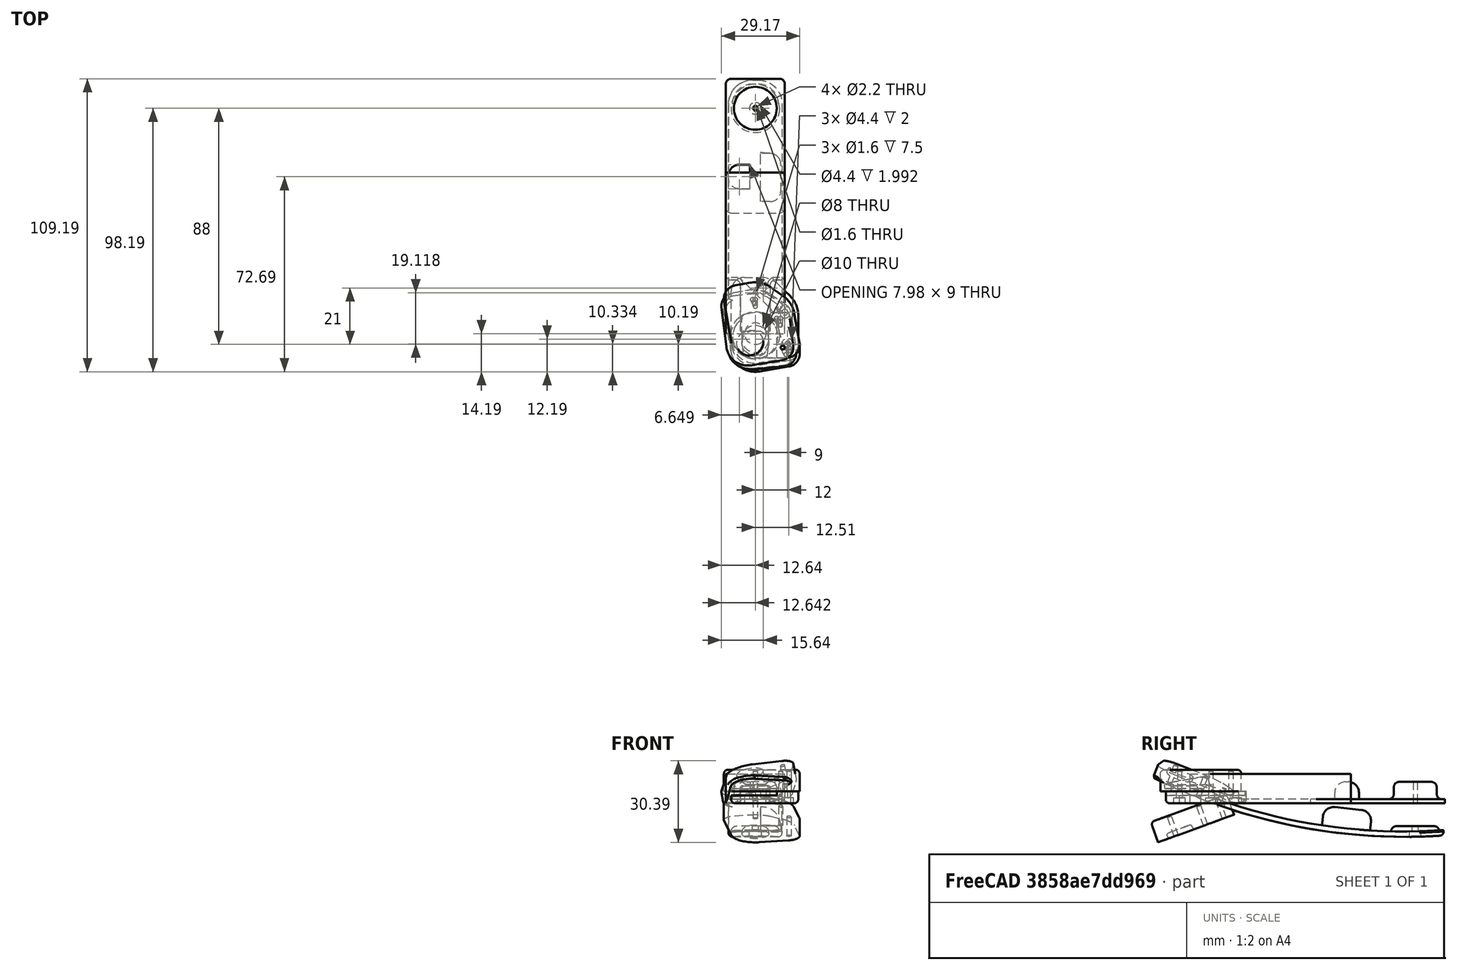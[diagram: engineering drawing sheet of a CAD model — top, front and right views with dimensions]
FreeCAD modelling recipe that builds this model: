
FCSTD DOCUMENT  (FreeCAD 1.0R38641 +678 (Git))
Label: HelmetVisir
License: All rights reserved
LicenseURL: https://en.wikipedia.org/wiki/All_rights_reserved
objects: Part::Fillet×37, Part::Cylinder×19, Part::Box×13, Part::MultiFuse×10, Part::Cut×10, Part::Chamfer×6, Part::Feature×4, Part::MultiCommon×1, Part::Mirroring×1
note: 101 computed .brp shape members not serialized (recipe doc carries the construction recipe); baked Part::Feature solids carry a one-line shape summary decoded from their .brp

FEATURE [Part::Cylinder] Cylinder012  label="Magnet001"
  Angle = 360
  AttacherType = Attacher::AttachEngine3D
  FirstAngle = 0
  Height = 6.5
  Radius = 5
  SecondAngle = 0
FEATURE [Part::Cylinder] Cylinder014  label="ScrewHolle008"
  Angle = 360
  AttacherType = Attacher::AttachEngine3D
  FirstAngle = 0
  Height = 12
  Placement = pos=(3,17,0) rot=(0,0,1;0rad)
  Radius = 0.8
  SecondAngle = 0
FEATURE [Part::Cylinder] Cylinder015  label="ScrewHolle009"
  Angle = 360
  AttacherType = Attacher::AttachEngine3D
  FirstAngle = 0
  Height = 12
  Placement = pos=(12,-4,0) rot=(0,0,1;0rad)
  Radius = 0.8
  SecondAngle = 0
FEATURE [Part::Cylinder] Cylinder023  label="ScrewHolle019"
  Angle = 360
  AttacherType = Attacher::AttachEngine3D
  FirstAngle = 0
  Height = 10
  Placement = pos=(0,84,5) rot=(-1,0,0;0rad)
  Radius = 1.1
  SecondAngle = 0
FEATURE [Part::Box] Box016  label="Cube016"
  AttacherType = Attacher::AttachEngine3D
  Height = 8
  Length = 22
  Placement = pos=(-11,-39,0) rot=(0,0,1;0rad)
  Width = 50
FEATURE [Part::Cylinder] Cylinder025  label="ScrewHolle022"
  Angle = 360
  AttacherType = Attacher::AttachEngine3D
  FirstAngle = 0
  Height = 12
  Placement = pos=(11,8,0) rot=(0,0,1;0rad)
  Radius = 0.8
  SecondAngle = 0
FEATURE [Part::Box] Box017  label="Cube017"
  AttacherType = Attacher::AttachEngine3D
  Height = 8
  Length = 25
  Placement = pos=(-9,-9,4.5) rot=(0,0,1;0rad)
  Width = 30
FEATURE [Part::Fillet] Fillet018
  Base = -> Box017
  EdgeLinks = -> Box017 [Edge1]
  Edges = 1 edges r=9: [Edge1]
FEATURE [Part::Fillet] Fillet019
  Base = -> Fillet018
  EdgeLinks = -> Fillet018 [Edge3,Edge15]
  Edges = 2 edges r=5: [Edge3,Edge15]
FEATURE [Part::Chamfer] Chamfer001
  Base = -> Fillet019
  EdgeLinks = -> Fillet019 [Edge19]
  Edges = 1 edges r=10: [Edge19]
FEATURE [Part::Fillet] Fillet020
  Base = -> Chamfer001
  EdgeLinks = -> Chamfer001 [Edge10,Edge13]
  Edges = 2 edges r=10: [Edge10,Edge13]
FEATURE [Part::Fillet] Fillet021
  Base = -> Fillet020
  EdgeLinks = -> Fillet020 [Edge4]
  Edges = 1 edges r=1.5: [Edge4]
FEATURE [Part::Box] Box  label="Cube"
  AttacherType = Attacher::AttachEngine3D
  Height = 4.5
  Length = 25
  Placement = pos=(-9,-9,0) rot=(0,0,1;0rad)
  Width = 30
FEATURE [Part::Fillet] Fillet001
  Base = -> Box
  EdgeLinks = -> Box [Edge1]
  Edges = 1 edges r=9: [Edge1]
FEATURE [Part::Fillet] Fillet002
  Base = -> Fillet001
  EdgeLinks = -> Fillet001 [Edge3,Edge15]
  Edges = 2 edges r=5: [Edge3,Edge15]
FEATURE [Part::Chamfer] Chamfer
  Base = -> Fillet002
  EdgeLinks = -> Fillet002 [Edge19]
  Edges = 1 edges r=10: [Edge19]
FEATURE [Part::Fillet] Fillet016
  Base = -> Chamfer
  EdgeLinks = -> Chamfer [Edge10,Edge13]
  Edges = 2 edges r=10: [Edge10,Edge13]
FEATURE [Part::Fillet] Fillet017
  Base = -> Fillet016
  EdgeLinks = -> Fillet016 [Edge22]
  Edges = 1 edges r=1.5: [Edge22]
FEATURE [Part::Cylinder] Cylinder011  label="ScrewHolle006"
  Angle = 360
  AttacherType = Attacher::AttachEngine3D
  FirstAngle = 0
  Height = 2
  Placement = pos=(3,17,0) rot=(0,0,1;0rad)
  Radius = 2.2
  SecondAngle = 0
FEATURE [Part::Cylinder] Cylinder008  label="ScrewHolle003"
  Angle = 360
  AttacherType = Attacher::AttachEngine3D
  FirstAngle = 0
  Height = 6.5
  Placement = pos=(3,17,0) rot=(0,0,1;0rad)
  Radius = 1.1
  SecondAngle = 0
FEATURE [Part::Cylinder] Cylinder026  label="ScrewHolle023"
  Angle = 360
  AttacherType = Attacher::AttachEngine3D
  FirstAngle = 0
  Height = 2
  Placement = pos=(11,8,0) rot=(0,0,1;0rad)
  Radius = 2.2
  SecondAngle = 0
FEATURE [Part::Cylinder] Cylinder024  label="ScrewHolle021"
  Angle = 360
  AttacherType = Attacher::AttachEngine3D
  FirstAngle = 0
  Height = 6.5
  Placement = pos=(11,8,0) rot=(0,0,1;0rad)
  Radius = 1.1
  SecondAngle = 0
FEATURE [Part::Cylinder] Cylinder009  label="ScrewHolle004"
  Angle = 360
  AttacherType = Attacher::AttachEngine3D
  FirstAngle = 0
  Height = 2
  Placement = pos=(12,-4,0) rot=(0,0,1;0rad)
  Radius = 2.2
  SecondAngle = 0
FEATURE [Part::Cylinder] Cylinder006  label="ScrewHolle001"
  Angle = 360
  AttacherType = Attacher::AttachEngine3D
  FirstAngle = 0
  Height = 6.5
  Placement = pos=(12,-4,0) rot=(0,0,1;0rad)
  Radius = 1.1
  SecondAngle = 0
FEATURE [Part::Feature] Fusion001  label="VisirBody001"
  shape: bbox 34 x 45 x 6.5 mm, 12 faces (baked)
FEATURE [Part::MultiFuse] Fusion
  Shapes = -> [Cylinder011,Cylinder008,Cylinder026,Cylinder024,Cylinder009,Cylinder006,Fusion001]
FEATURE [Part::Cut] Cut  label="ClipCap"
  Base = -> Fillet017
  Tool = -> Fusion
FEATURE [Part::Fillet] Fillet022
  Base = -> Cylinder012
  EdgeLinks = -> Cylinder012 [Edge3]
  Edges = 1 edges r=1: [Edge3]
FEATURE [Part::MultiFuse] Fusion010
  Shapes = -> [Fillet022,Cylinder014,Cylinder025,Cylinder015]
FEATURE [Part::Cylinder] Cylinder027  label="Axis"
  Angle = 360
  AttacherType = Attacher::AttachEngine3D
  FirstAngle = 0
  Height = 3
  Placement = pos=(0,84,8.5) rot=(-1,0,0;0rad)
  Radius = 9
  SecondAngle = 0
FEATURE [Part::Fillet] Fillet024
  Base = -> Cylinder027
  EdgeLinks = -> Cylinder027 [Edge2]
  Edges = 1 edges r=2: [Edge2]
FEATURE [Part::Cylinder] Cylinder028  label="Axis001"
  Angle = 360
  AttacherType = Attacher::AttachEngine3D
  FirstAngle = 0
  Height = 3
  Placement = pos=(0,84,10.5) rot=(-1,0,0;0rad)
  Radius = 2.2
  SecondAngle = 0
FEATURE [Part::MultiFuse] Fusion011  label="AxisScrewHolle"
  Shapes = -> [Cylinder023,Cylinder028]
FEATURE [Part::Cylinder] Cylinder  label="AxisHolle"
  Angle = 360
  AttacherType = Attacher::AttachEngine3D
  FirstAngle = 0
  Height = 10
  Radius = 0.8
  SecondAngle = 0
FEATURE [Part::Box] Box018  label="Cube018"
  AttacherType = Attacher::AttachEngine3D
  Height = 8
  Length = 22
  Placement = pos=(-11,-39,1.5) rot=(0,0,1;0rad)
  Width = 50
FEATURE [Part::Cylinder] Cylinder029  label="AxisHolle001"
  Angle = 360
  AttacherType = Attacher::AttachEngine3D
  FirstAngle = 0
  Height = 10
  Radius = 8
  SecondAngle = 0
FEATURE [Part::Cut] Cut008
  Base = -> Box018
  Tool = -> Cylinder029
FEATURE [Part::Fillet] Fillet025
  Base = -> Cut008
  EdgeLinks = -> Cut008 [Edge14]
  Edges = 1 edges r=2: [Edge14]
FEATURE [Part::Fillet] Fillet026
  Base = -> Box016
  EdgeLinks = -> Box016 [Edge1,Edge3,Edge5,Edge7]
  Edges = 4 edges r=2: [Edge1,Edge3,Edge5,Edge7]
FEATURE [Part::MultiFuse] Fusion014
  Shapes = -> [Fillet025,Cylinder]
FEATURE [Part::Cut] Cut009
  Base = -> Fillet026
  Tool = -> Fusion014
FEATURE [Part::Box] Box019  label="Cube019"
  AttacherType = Attacher::AttachEngine3D
  Height = 8
  Length = 8
  Placement = pos=(-10,-30,0) rot=(0,0,1;0rad)
  Width = 9
FEATURE [Part::Fillet] Fillet029
  Base = -> Cut009
  EdgeLinks = -> Cut009 [Edge32]
  Edges = 1 edges r=2: [Edge32]
FEATURE [Part::Box] Box020  label="Cube020"
  AttacherType = Attacher::AttachEngine3D
  Height = 9
  Length = 7.5
  Placement = pos=(2,50,1) rot=(1,0,0;0.10472rad)
  Width = 18
FEATURE [Part::Fillet] Fillet030
  Base = -> Box020
  EdgeLinks = -> Box020 [Edge8]
  Edges = 1 edges r=7: [Edge8]
FEATURE [Part::Fillet] Fillet031  label="Tooth"
  Base = -> Fillet030
  EdgeLinks = -> Fillet030 [Edge6,Edge10]
  Edges = 2 edges r=4: [Edge6,Edge10]
FEATURE [Part::Cut] Cut010  label="Claw_000"
  Base = -> Fillet021
  Placement = pos=(0,-2,0) rot=(0,0,1;0.174533rad)
  Tool = -> Fusion010
FEATURE [Part::Feature] Cut012  label="Claw_001"
  Placement = pos=(0,0,-15) rot=(1,0,0;0.349066rad)
  shape: bbox 28.9 x 31.12 x 17.51 mm, 31 faces (baked)
FEATURE [Part::Feature] Cut014  label="Claw_002"
  Placement = pos=(0,0,0) rot=(0,1,0;0.174533rad)
  shape: bbox 28.25 x 31.12 x 19.61 mm, 31 faces (baked)
FEATURE [Part::Cylinder] Cylinder030  label="Cylinder"
  Angle = 24
  AttacherType = Attacher::AttachEngine3D
  FirstAngle = 0
  Height = 20
  Placement = pos=(-10,0,0) rot=(0,1,0;1.5708rad)
  Radius = 210
  SecondAngle = 0
FEATURE [Part::Cylinder] Cylinder032
  Angle = 40
  AttacherType = Attacher::AttachEngine3D
  FirstAngle = 0
  Height = 20
  Placement = pos=(-10,0,0) rot=(0,1,0;1.5708rad)
  Radius = 208
  SecondAngle = 0
FEATURE [Part::Cut] Cut015
  Base = -> Cylinder030
  Placement = pos=(0,80,-197.5) rot=(1,0,0;3.07178rad)
  Tool = -> Cylinder032
FEATURE [Part::Fillet] Fillet
  Base = -> Cut015
  EdgeLinks = -> Cut015 [Edge8,Edge10]
  Edges = 2 edges r=9: [Edge8,Edge10]
FEATURE [Part::Fillet] Fillet034
  Base = -> Fillet
  EdgeLinks = -> Fillet [Edge14,Edge16]
  Edges = 2 edges r=2: [Edge14,Edge16]
FEATURE [Part::Fillet] Fillet035
  Base = -> Fillet034
  EdgeLinks = -> Fillet034 [Edge8]
  Edges = 1 edges r=1.5: [Edge8]
FEATURE [Part::MultiFuse] Fusion016
  Shapes = -> [Fillet035,Fillet024]
FEATURE [Part::Cut] Cut016
  Base = -> Fusion016
  Tool = -> Fusion011
FEATURE [Part::Fillet] Fillet036
  Base = -> Fillet031
  EdgeLinks = -> Fillet031 [Edge4]
  Edges = 1 edges r=1: [Edge4]
FEATURE [Part::Cylinder] Cylinder033
  Angle = 360
  AttacherType = Attacher::AttachEngine3D
  FirstAngle = 0
  Height = 33
  Placement = pos=(-15,80,-197.5) rot=(0,1,0;1.5708rad)
  Radius = 210
  SecondAngle = 0
FEATURE [Part::MultiCommon] Common
  Shapes = -> [Cut014,Cylinder033]
FEATURE [Part::Fillet] Fillet037
  Base = -> Common
  EdgeLinks = -> Common [Edge21]
  Edges = 1 edges r=1: [Edge21]
FEATURE [Part::MultiFuse] Fusion017  label="HandlePassive"
  Shapes = -> [Cut016,Fillet036,Fillet037]
FEATURE [Part::Fillet] Fillet027
  Base = -> Box019
  EdgeLinks = -> Box019 [Edge2]
  Edges = 1 edges r=7: [Edge2]
FEATURE [Part::Fillet] Fillet028
  Base = -> Fillet027
  EdgeLinks = -> Fillet027 [Edge6,Edge10]
  Edges = 2 edges r=4: [Edge6,Edge10]
FEATURE [Part::MultiFuse] Fusion015  label="Hindge"
  Placement = pos=(0,84,0) rot=(0,0,1;0rad)
  Shapes = -> [Fillet029,Fillet028]
FEATURE [Part::Box] Box021  label="Cube021"
  AttacherType = Attacher::AttachEngine3D
  Height = 7
  Length = 22
  Placement = pos=(-11,0,0) rot=(0,0,1;0rad)
  Width = 60
FEATURE [Part::Cylinder] Cylinder034
  Angle = 360
  AttacherType = Attacher::AttachEngine3D
  FirstAngle = 0
  Height = 4.5
  Placement = pos=(0,0,4.5) rot=(1,0,0;0.174533rad)
  Radius = 9
  SecondAngle = 0
FEATURE [Part::Mirroring] Part__Mirroring  label="HandlePassive (Mirror #1)"
  Base = (0,0,0)
  Normal = (0,0,1)
  Source = -> Fusion017
FEATURE [Part::Box] Box022  label="Cube022"
  AttacherType = Attacher::AttachEngine3D
  Height = 11
  Length = 22
  Placement = pos=(-11,0,0) rot=(0,0,1;0rad)
  Width = 60
FEATURE [Part::Box] Box023  label="Cube023"
  AttacherType = Attacher::AttachEngine3D
  Height = 11
  Length = 5.5
  Placement = pos=(-11,-10,0) rot=(0,0,1;0rad)
  Width = 30
FEATURE [Part::Box] Box024  label="Cube024"
  AttacherType = Attacher::AttachEngine3D
  Height = 11
  Length = 5.5
  Placement = pos=(5.5,-10,0) rot=(0,0,1;0rad)
  Width = 30
FEATURE [Part::Box] Box025  label="Cube025"
  AttacherType = Attacher::AttachEngine3D
  Height = 12
  Length = 22
  Placement = pos=(-11,4,1.5) rot=(0,0,1;0rad)
  Width = 60
FEATURE [Part::Chamfer] Chamfer003
  Base = -> Box025
  EdgeLinks = -> Box025 [Edge9]
  Edges = 1 edges r=11: [Edge9]
FEATURE [Part::Fillet] Fillet040
  Base = -> Chamfer003
  EdgeLinks = -> Chamfer003 [Edge9]
  Edges = 1 edges r=14: [Edge9]
FEATURE [Part::Box] Box026  label="Cube026"
  AttacherType = Attacher::AttachEngine3D
  Height = 11
  Length = 22
  Placement = pos=(-11,-15,-6) rot=(0,0,1;0rad)
  Width = 34
FEATURE [Part::Chamfer] Chamfer004
  Base = -> Box026
  EdgeLinks = -> Box026 [Edge12]
  Edges = 1 edges r=10: [Edge12]
FEATURE [Part::Fillet] Fillet041  label="BottomCut001"
  Base = -> Chamfer004
  EdgeLinks = -> Chamfer004 [Edge6]
  Edges = 1 edges r=14: [Edge6]
FEATURE [Part::MultiFuse] Fusion019
  Shapes = -> [Fillet041,Fillet040]
FEATURE [Part::Fillet] Fillet044
  Base = -> Box024
  EdgeLinks = -> Box024 [Edge3]
  Edges = 1 edges r=2: [Edge3]
FEATURE [Part::Fillet] Fillet045
  Base = -> Box023
  EdgeLinks = -> Box023 [Edge7]
  Edges = 1 edges r=2: [Edge7]
FEATURE [Part::Fillet] Fillet051
  Base = -> Box021
  EdgeLinks = -> Box021 [Edge3,Edge7]
  Edges = 2 edges r=2: [Edge3,Edge7]
FEATURE [Part::Fillet] Fillet052
  Base = -> Fillet044
  EdgeLinks = -> Fillet044 [Edge6]
  Edges = 1 edges r=10: [Edge6]
FEATURE [Part::Fillet] Fillet053
  Base = -> Fillet045
  EdgeLinks = -> Fillet045 [Edge8]
  Edges = 1 edges r=10: [Edge8]
FEATURE [Part::MultiFuse] Fusion022  label="SideCut001"
  Shapes = -> [Fillet052,Fillet053]
FEATURE [Part::Feature] Fillet054  label="BottomCut002"
  Placement = pos=(0,0,-3) rot=(0,0,1;0rad)
  shape: bbox 22 x 34 x 11 mm, 8 faces (baked)
FEATURE [Part::Cut] Cut017
  Base = -> Fillet051
  Tool = -> Fusion019
FEATURE [Part::Fillet] Fillet058
  Base = -> Cylinder034
  EdgeLinks = -> Cylinder034 [Edge3]
  Edges = 1 edges r=1: [Edge3]
FEATURE [Part::Chamfer] Chamfer005
  Base = -> Fillet058
  EdgeLinks = -> Fillet058 [Edge3]
  Edges = 1 edges r=1.5: [Edge3]
FEATURE [Part::Fillet] Fillet059
  Base = -> Chamfer005
  EdgeLinks = -> Chamfer005 [Edge2]
  Edges = 1 edges r=4: [Edge2]
FEATURE [Part::Cut] Cut021
  Base = -> Fillet059
  Tool = -> Fillet054
FEATURE [Part::Fillet] Fillet060
  Base = -> Cut017
  EdgeLinks = -> Cut017 [Edge11]
  Edges = 1 edges r=16: [Edge11]
FEATURE [Part::Fillet] Fillet061
  Base = -> Fillet060
  EdgeLinks = -> Fillet060 [Edge31]
  Edges = 1 edges r=15: [Edge31]
FEATURE [Part::Cut] Cut022
  Base = -> Fillet061
  Tool = -> Fusion022
FEATURE [Part::Fillet] Fillet062
  Base = -> Cut022
  EdgeLinks = -> Cut022 [Edge1,Edge48]
  Edges = 2 edges r=2: [Edge1,Edge48]
FEATURE [Part::Chamfer] Chamfer006
  Base = -> Fillet062
  EdgeLinks = -> Fillet062 [Edge59]
  Edges = 1 edges r=1.5: [Edge59]
FEATURE [Part::Fillet] Fillet063
  Base = -> Chamfer006
  EdgeLinks = -> Chamfer006 [Edge10]
  Edges = 1 edges r=2: [Edge10]
FEATURE [Part::Fillet] Fillet064
  Base = -> Fillet063
  EdgeLinks = -> Fillet063 [Edge39]
  Edges = 1 edges r=1: [Edge39]
FEATURE [Part::Box] Box027  label="Cube027"
  AttacherType = Attacher::AttachEngine3D
  Height = 10
  Length = 10
  Placement = pos=(-5,-10,7) rot=(0,0,1;0rad)
  Width = 20
FEATURE [Part::Fillet] Fillet065
  Base = -> Box027
  EdgeLinks = -> Box027 [Edge4,Edge8]
  Edges = 2 edges r=2: [Edge4,Edge8]
FEATURE [Part::Cut] Cut023
  Base = -> Cut021
  Tool = -> Fillet065
FEATURE [Part::MultiFuse] Fusion023  label="Button"
  Shapes = -> [Cut023,Fillet064]
